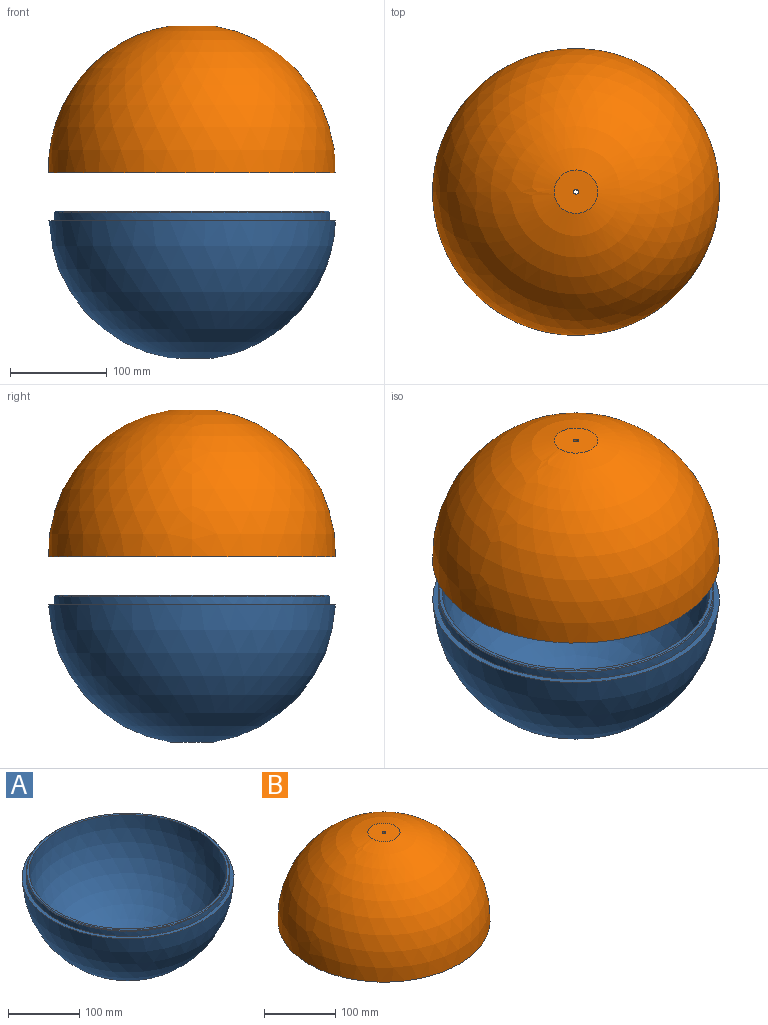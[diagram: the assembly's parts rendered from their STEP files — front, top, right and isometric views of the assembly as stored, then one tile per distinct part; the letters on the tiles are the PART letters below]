
ASSEMBLY  parts=2 mates=1
PART A: 8 faces, bbox 296.8x296.8x151.8 mm
  f0: sphere r=138.5mm, area 124856.3mm2, adj f1,f7
  f1: plane 283.5x283.5mm, normal (0,0,1), area 2939.9mm2, adj f0,f6
  f2: cylinder r=142.75mm len=285.5mm, axis (0,0,1), area 8072.3mm2, adj f3,f6
  f3: plane 296.83x296.83mm, normal (0,0,1), area 5182.6mm2, adj f2,f4
  f4: sphere r=148.5mm, area 132293.4mm2, adj f3,f5
  f5: plane 45x45mm, normal (0,0,-1), area 1570mm2, adj f4,f7
  f6: cone r=141.75mm half-angle=45deg, axis (0,0,-1), area 1264mm2, adj f1,f2
  f7: cylinder r=2.55mm len=8.31mm, axis (0,0,-1), area 133.3mm2, adj f0,f5
PART B: 8 faces, bbox 297x297x151.8 mm
  f0: sphere r=138.5mm, area 116154.1mm2, adj f2,f7
  f1: cylinder r=144.25mm len=288.5mm, axis (0,0,-1), area 8157.1mm2, adj f2,f6
  f2: plane 288.5x288.5mm, normal (0,0,-1), area 5186.2mm2, adj f0,f1
  f3: plane 45x45mm, normal (0,0,1), area 1570mm2, adj f4,f7
  f4: sphere r=148.5mm, area 141624mm2, adj f3,f5
  f5: plane 296.83x296.83mm, normal (0,0,-1), area 2920.7mm2, adj f4,f6
  f6: cone r=144.25mm half-angle=45deg, axis (0,0,-1), area 1286.2mm2, adj f1,f5
  f7: cylinder r=2.55mm len=8.31mm, axis (0,0,1), area 133.3mm2, adj f0,f3
PLACE A at identity
PLACE B t=(0,0,50)mm
MATE revolute B.f7 <-> A.f6  axis (0,0,1) through (0,0,50)mm
